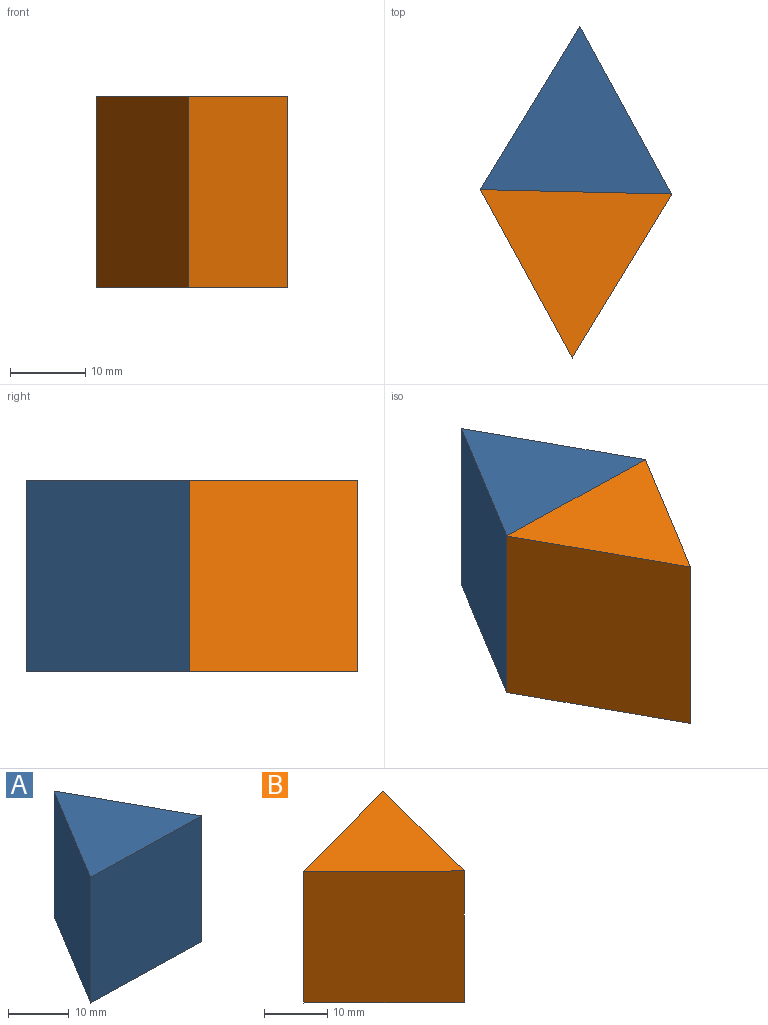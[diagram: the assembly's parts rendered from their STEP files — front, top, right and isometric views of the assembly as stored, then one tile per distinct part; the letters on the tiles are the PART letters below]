
ASSEMBLY  parts=2 mates=1
PART A: 5 faces, bbox 25.4x22.3x25.4 mm
  f0: plane 25.4x22.28mm, normal (0.88,0.48,0), area 645.2mm2, adj f1,f2,f3,f4
  f1: plane 25.4x21.7mm, normal (-0.85,0.52,0), area 645.2mm2, adj f0,f2,f3,f4
  f2: plane 25.4x25.39mm, normal (-0.02,-1,0), area 645.2mm2, adj f0,f1,f3,f4
  f3: plane 25.39x22.28mm, normal (0,0,1), area 279.4mm2, adj f0,f1,f2
  f4: plane 25.39x22.28mm, normal (0,0,-1), area 279.4mm2, adj f0,f1,f2
PART B: 5 faces, bbox 24.5x24.6x25.4 mm
  f0: plane 25.4x24.47mm, normal (-0.27,0.96,0), area 645.2mm2, adj f1,f2,f3,f4
  f1: plane 25.4x18.12mm, normal (-0.7,-0.71,0), area 645.2mm2, adj f0,f2,f3,f4
  f2: plane 25.4x24.59mm, normal (0.97,-0.25,0), area 645.2mm2, adj f0,f1,f3,f4
  f3: plane 24.59x24.47mm, normal (0,0,1), area 279.4mm2, adj f0,f1,f2
  f4: plane 24.59x24.47mm, normal (0,0,-1), area 279.4mm2, adj f0,f1,f2
PLACE A t=(3.28,10.7,6.03)mm
PLACE B rot(axis=(0,0,-1),16.8deg) t=(9.74,15.56,6.03)mm
MATE fastened B.f0 <-> A.f2  axis (0.02,1,0) through (3.11,24.95,18.73)mm
